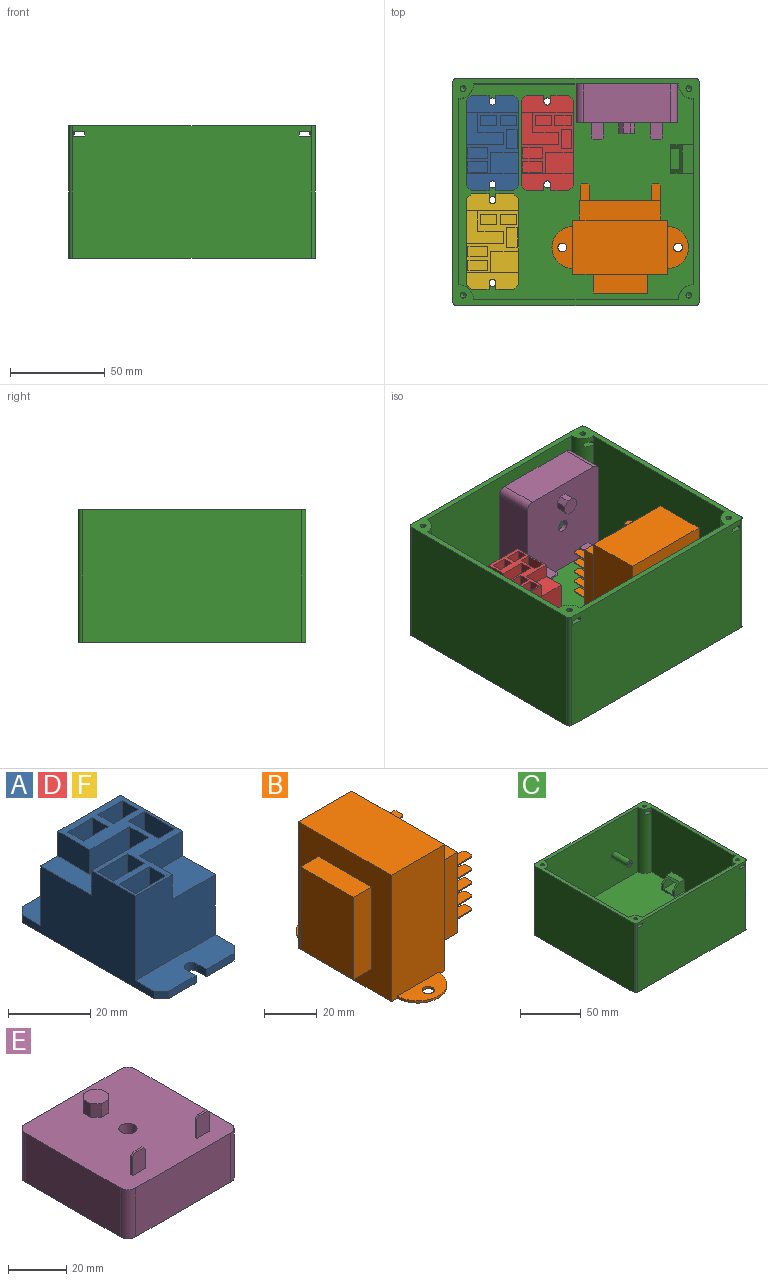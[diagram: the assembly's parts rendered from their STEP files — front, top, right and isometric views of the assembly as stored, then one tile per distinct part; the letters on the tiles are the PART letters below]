
ASSEMBLY  parts=6 mates=8
PART A: 55 faces, bbox 27.4x50.3x27.3 mm
  f0: plane 9.42x2.2mm, normal (0,-1,0), area 20.7mm2, adj f2,f9,f14,f54
  f1: plane 9.42x2.2mm, normal (0,1,0), area 20.7mm2, adj f3,f9,f13,f50
  f2: plane 27.43x8.89mm, normal (0,0,1), area 220.5mm2, adj f0,f5,f6,f7,f10,f14,f15,f52
  f3: plane 27.43x8.89mm, normal (0,0,1), area 220.5mm2, adj f1,f5,f6,f8,f11,f12,f13,f49
  f4: plane 32.51x27.43mm, normal (0,0,1), area 270.6mm2, adj f5,f6,f7,f8,f16,f17,f18,f19
  f5: plane 45.29x27.3mm, normal (1,0,0), area 833.8mm2, adj f2,f3,f4,f7,f8,f9,f13,f14
  f6: plane 45.29x27.3mm, normal (-1,0,0), area 789mm2, adj f2,f3,f4,f7,f8,f9,f12,f15
  f7: plane 27.43x25.1mm, normal (0,-1,0), area 581mm2, adj f2,f4,f5,f6,f21,f23
  f8: plane 27.43x25.1mm, normal (0,1,0), area 645.2mm2, adj f3,f4,f5,f6,f17,f20
  f9: plane 50.29x27.43mm, normal (0,0,-1), area 1332.8mm2, adj f0,f1,f5,f6,f10,f11,f12,f13
  f10: plane 9.42x2.2mm, normal (0,-1,0), area 20.7mm2, adj f2,f9,f15,f53
  f11: plane 9.42x2.2mm, normal (0,1,0), area 20.7mm2, adj f3,f9,f12,f51
  f12: plane 2.5x2.5mm, normal (-0.71,0.71,0), area 7.8mm2, adj f3,f6,f9,f11
  f13: plane 2.5x2.5mm, normal (0.71,0.71,0), area 7.8mm2, adj f1,f3,f5,f9
  f14: plane 2.5x2.5mm, normal (0.71,-0.71,0), area 7.8mm2, adj f0,f2,f5,f9
  f15: plane 2.5x2.5mm, normal (-0.71,-0.71,0), area 7.8mm2, adj f2,f6,f9,f10
  f16: plane 13.7x7.3mm, normal (0,-1,0), area 100mm2, adj f4,f17,f19,f20
  f17: plane 10.96x7.3mm, normal (-1,0,0), area 80mm2, adj f4,f8,f16,f20
  f18: plane 19.63x7.3mm, normal (0,1,0), area 143.3mm2, adj f4,f6,f19,f20
  f19: plane 7.3x6.4mm, normal (-1,0,0), area 46.7mm2, adj f4,f16,f18,f20
  f20: plane 19.63x17.36mm, normal (0,0,1), area 190.7mm2, adj f6,f8,f16,f17,f18,f19
  f21: plane 11.21x7.3mm, normal (1,0,0), area 81.8mm2, adj f4,f7,f22,f23
  f22: plane 14.73x7.3mm, normal (0,-1,0), area 107.5mm2, adj f4,f5,f21,f23
  f23: plane 14.73x11.21mm, normal (0,0,1), area 165.2mm2, adj f5,f7,f21,f22
  f24: plane 7.3x5.3mm, normal (1,0,0), area 38.7mm2, adj f4,f25,f27,f28
  f25: plane 8.5x7.3mm, normal (0,1,0), area 62.1mm2, adj f4,f24,f26,f28
  f26: plane 7.3x5.3mm, normal (-1,0,0), area 38.7mm2, adj f4,f25,f27,f28
  f27: plane 8.5x7.3mm, normal (0,-1,0), area 62.1mm2, adj f4,f24,f26,f28
  f28: plane 8.5x5.3mm, normal (0,0,1), area 45.1mm2, adj f24,f25,f26,f27
  f29: plane 8.5x7.3mm, normal (0,-1,0), area 62.1mm2, adj f4,f30,f32,f33
  f30: plane 7.3x5.3mm, normal (1,0,0), area 38.7mm2, adj f4,f29,f31,f33
  f31: plane 8.5x7.3mm, normal (0,1,0), area 62.1mm2, adj f4,f30,f32,f33
  f32: plane 7.3x5.3mm, normal (-1,0,0), area 38.7mm2, adj f4,f29,f31,f33
  f33: plane 8.5x5.3mm, normal (0,0,1), area 45.1mm2, adj f29,f30,f31,f32
  f34: plane 7.3x5.6mm, normal (0,1,0), area 40.9mm2, adj f4,f35,f37,f38
  f35: plane 10.3x7.3mm, normal (-1,0,0), area 75.2mm2, adj f4,f34,f36,f38
  f36: plane 7.3x5.6mm, normal (0,-1,0), area 40.9mm2, adj f4,f35,f37,f38
  f37: plane 10.3x7.3mm, normal (1,0,0), area 75.2mm2, adj f4,f34,f36,f38
  f38: plane 10.3x5.6mm, normal (0,0,1), area 57.7mm2, adj f34,f35,f36,f37
  f39: plane 10.5x7.3mm, normal (0,-1,0), area 76.7mm2, adj f4,f40,f42,f43
  f40: plane 7.3x5.6mm, normal (1,0,0), area 40.9mm2, adj f4,f39,f41,f43
  f41: plane 10.5x7.3mm, normal (0,1,0), area 76.6mm2, adj f4,f40,f42,f43
  f42: plane 7.3x5.6mm, normal (-1,0,0), area 40.9mm2, adj f4,f39,f41,f43
  f43: plane 10.5x5.6mm, normal (0,0,1), area 58.8mm2, adj f39,f40,f41,f42
  f44: plane 10.5x7.3mm, normal (0,-1,0), area 76.7mm2, adj f4,f45,f47,f48
  f45: plane 7.3x5.6mm, normal (1,0,0), area 40.9mm2, adj f4,f44,f46,f48
  f46: plane 10.5x7.3mm, normal (0,1,0), area 76.7mm2, adj f4,f45,f47,f48
  f47: plane 7.3x5.6mm, normal (-1,0,0), area 40.9mm2, adj f4,f44,f46,f48
  f48: plane 10.5x5.6mm, normal (0,0,1), area 58.8mm2, adj f44,f45,f46,f47
  f49: cylinder r=1.8mm len=3.6mm, axis (0,0,-1), area 12.4mm2, adj f3,f9,f50,f51
  f50: plane 3.35x2.2mm, normal (-1,0,0), area 7.4mm2, adj f1,f3,f9,f49
  f51: plane 3.35x2.2mm, normal (1,0,0), area 7.4mm2, adj f3,f9,f11,f49
  f52: cylinder r=1.8mm len=3.6mm, axis (0,0,-1), area 12.4mm2, adj f2,f9,f53,f54
  f53: plane 3.35x2.2mm, normal (1,0,0), area 7.4mm2, adj f2,f9,f10,f52
  f54: plane 3.35x2.2mm, normal (-1,0,0), area 7.4mm2, adj f0,f2,f9,f52
PART B: 92 faces, bbox 57.7x72x58.8 mm
  f0: plane 58.75x49.85mm, normal (1,0,0), area 1316.2mm2, adj f1,f3,f4,f5,f17,f18,f19,f20
  f1: plane 58.75x28.65mm, normal (0,1,0), area 1661.1mm2, adj f0,f2,f4,f5,f10,f11
  f2: plane 58.75x49.85mm, normal (-1,0,0), area 1838.6mm2, adj f1,f3,f4,f5,f12,f13,f14,f15
  f3: plane 58.75x28.65mm, normal (0,-1,0), area 1661.1mm2, adj f0,f2,f4,f5,f6,f8
  f4: plane 49.85x28.65mm, normal (0,0,1), area 1428.2mm2, adj f0,f1,f2,f3
  f5: plane 71.95x28.65mm, normal (0,0,-1), area 1777.1mm2, adj f0,f1,f2,f3,f6,f7,f9,f10
  f6: cylinder r=11.05mm len=22.1mm, axis (0,0,-1), area 34.7mm2, adj f3,f5,f8
  f7: cylinder r=2.35mm len=4.7mm, axis (0,0,-1), area 14.8mm2, adj f5,f8
  f8: plane 22.1x11.05mm, normal (0,0,1), area 174.4mm2, adj f3,f6,f7
  f9: cylinder r=2.35mm len=4.7mm, axis (0,0,-1), area 14.8mm2, adj f5,f11
  f10: cylinder r=11.05mm len=22.1mm, axis (0,0,-1), area 34.7mm2, adj f1,f5,f11
  f11: plane 22.1x11.05mm, normal (0,0,1), area 174.4mm2, adj f1,f9,f10
  f12: plane 38.25x9.75mm, normal (0,-1,0), area 372.9mm2, adj f2,f13,f15,f16
  f13: plane 28.5x9.75mm, normal (0,0,1), area 277.9mm2, adj f2,f12,f14,f16
  f14: plane 38.25x9.75mm, normal (0,1,0), area 372.9mm2, adj f2,f13,f15,f16
  f15: plane 28.5x9.75mm, normal (0,0,-1), area 277.9mm2, adj f2,f12,f14,f16
  f16: plane 38.25x28.5mm, normal (-1,0,0), area 1090.1mm2, adj f12,f13,f14,f15
  f17: plane 37.5x10.5mm, normal (0,1,0), area 393.8mm2, adj f0,f18,f20,f21
  f18: plane 43x10.5mm, normal (0,0,1), area 451.5mm2, adj f0,f17,f19,f21
  f19: plane 37.5x10.5mm, normal (0,-1,0), area 393.8mm2, adj f0,f18,f20,f21
  f20: plane 43x10.5mm, normal (0,0,-1), area 451.5mm2, adj f0,f17,f19,f21
  f21: plane 43x37.5mm, normal (1,0,0), area 1588.5mm2, adj f17,f18,f19,f20,f22,f23,f24,f25
  f22: plane 8x0.5mm, normal (0,1,0), area 4mm2, adj f21,f23,f25,f86
  f23: plane 8.75x4.8mm, normal (0,0,1), area 41.4mm2, adj f21,f22,f24,f26,f86,f87
  f24: plane 8x0.5mm, normal (0,-1,0), area 4mm2, adj f21,f23,f25,f87
  f25: plane 8.75x4.8mm, normal (0,0,-1), area 41.4mm2, adj f21,f22,f24,f26,f86,f87
  f26: plane 3.3x0.5mm, normal (1,0,0), area 1.6mm2, adj f23,f25,f86,f87
  f27: plane 8.75x4.8mm, normal (0,0,-1), area 41.4mm2, adj f21,f28,f30,f31,f88,f89
  f28: plane 8x0.5mm, normal (0,1,0), area 4mm2, adj f21,f27,f29,f88
  f29: plane 8.75x4.8mm, normal (0,0,1), area 41.4mm2, adj f21,f28,f30,f31,f88,f89
  f30: plane 8x0.5mm, normal (0,-1,0), area 4mm2, adj f21,f27,f29,f89
  f31: plane 3.3x0.5mm, normal (1,0,0), area 1.7mm2, adj f27,f29,f88,f89
  f32: plane 8.75x4.8mm, normal (0,0,-1), area 41.4mm2, adj f21,f33,f35,f36,f90,f91
  f33: plane 8x0.5mm, normal (0,1,0), area 4mm2, adj f21,f32,f34,f90
  f34: plane 8.75x4.8mm, normal (0,0,1), area 41.4mm2, adj f21,f33,f35,f36,f90,f91
  f35: plane 8x0.5mm, normal (0,-1,0), area 4mm2, adj f21,f32,f34,f91
  f36: plane 3.3x0.5mm, normal (1,0,0), area 1.7mm2, adj f32,f34,f90,f91
  f37: plane 8x0.5mm, normal (0,1,0), area 4mm2, adj f21,f38,f40,f84
  f38: plane 8.75x4.8mm, normal (0,0,1), area 41.4mm2, adj f21,f37,f39,f41,f84,f85
  f39: plane 8x0.5mm, normal (0,-1,0), area 4mm2, adj f21,f38,f40,f85
  f40: plane 8.75x4.8mm, normal (0,0,-1), area 41.4mm2, adj f21,f37,f39,f41,f84,f85
  f41: plane 3.3x0.5mm, normal (1,0,0), area 1.7mm2, adj f38,f40,f84,f85
  f42: plane 8x0.5mm, normal (0,1,0), area 4mm2, adj f21,f43,f45,f75
  f43: plane 8.75x4.8mm, normal (0,0,1), area 41.4mm2, adj f21,f42,f44,f46,f74,f75
  f44: plane 8x0.5mm, normal (0,-1,0), area 4mm2, adj f21,f43,f45,f74
  f45: plane 8.75x4.8mm, normal (0,0,-1), area 41.4mm2, adj f21,f42,f44,f46,f74,f75
  f46: plane 3.3x0.5mm, normal (1,0,0), area 1.7mm2, adj f43,f45,f74,f75
  f47: plane 8x0.5mm, normal (0,-1,0), area 4mm2, adj f21,f48,f50,f81
  f48: plane 8.75x4.8mm, normal (0,0,-1), area 41.4mm2, adj f21,f47,f49,f51,f80,f81
  f49: plane 8x0.5mm, normal (0,1,0), area 4mm2, adj f21,f48,f50,f80
  f50: plane 8.75x4.8mm, normal (0,0,1), area 41.4mm2, adj f21,f47,f49,f51,f80,f81
  f51: plane 3.3x0.5mm, normal (1,0,0), area 1.6mm2, adj f48,f50,f80,f81
  f52: plane 8x0.5mm, normal (0,-1,0), area 4mm2, adj f21,f53,f55,f79
  f53: plane 8.75x4.8mm, normal (0,0,-1), area 41.4mm2, adj f21,f52,f54,f56,f78,f79
  f54: plane 8x0.5mm, normal (0,1,0), area 4mm2, adj f21,f53,f55,f78
  f55: plane 8.75x4.8mm, normal (0,0,1), area 41.4mm2, adj f21,f52,f54,f56,f78,f79
  f56: plane 3.3x0.5mm, normal (1,0,0), area 1.7mm2, adj f53,f55,f78,f79
  f57: plane 8.75x4.8mm, normal (0,0,1), area 41.4mm2, adj f21,f58,f60,f61,f82,f83
  f58: plane 8x0.5mm, normal (0,-1,0), area 4mm2, adj f21,f57,f59,f83
  f59: plane 8.75x4.8mm, normal (0,0,-1), area 41.4mm2, adj f21,f58,f60,f61,f82,f83
  f60: plane 8x0.5mm, normal (0,1,0), area 4mm2, adj f21,f57,f59,f82
  f61: plane 3.3x0.5mm, normal (1,0,0), area 1.7mm2, adj f57,f59,f82,f83
  f62: plane 8x0.5mm, normal (0,1,0), area 4mm2, adj f21,f63,f65,f72
  f63: plane 8.75x4.8mm, normal (0,0,1), area 41.4mm2, adj f21,f62,f64,f66,f72,f73
  f64: plane 8x0.5mm, normal (0,-1,0), area 4mm2, adj f21,f63,f65,f73
  f65: plane 8.75x4.8mm, normal (0,0,-1), area 41.4mm2, adj f21,f62,f64,f66,f72,f73
  f66: plane 3.3x0.5mm, normal (1,0,0), area 1.7mm2, adj f63,f65,f72,f73
  f67: plane 8x0.5mm, normal (0,-1,0), area 4mm2, adj f21,f68,f70,f77
  f68: plane 8.75x4.8mm, normal (0,0,-1), area 41.4mm2, adj f21,f67,f69,f71,f76,f77
  f69: plane 8x0.5mm, normal (0,1,0), area 4mm2, adj f21,f68,f70,f76
  f70: plane 8.75x4.8mm, normal (0,0,1), area 41.4mm2, adj f21,f67,f69,f71,f76,f77
  f71: plane 3.3x0.5mm, normal (1,0,0), area 1.7mm2, adj f68,f70,f76,f77
  f72: plane 0.75x0.75mm, normal (0.71,0.71,0), area 0.5mm2, adj f62,f63,f65,f66
  f73: plane 0.75x0.75mm, normal (0.71,-0.71,0), area 0.5mm2, adj f63,f64,f65,f66
  f74: plane 0.75x0.75mm, normal (0.71,-0.71,0), area 0.5mm2, adj f43,f44,f45,f46
  f75: plane 0.75x0.75mm, normal (0.71,0.71,0), area 0.5mm2, adj f42,f43,f45,f46
  f76: plane 0.75x0.75mm, normal (0.71,0.71,0), area 0.5mm2, adj f68,f69,f70,f71
  f77: plane 0.75x0.75mm, normal (0.71,-0.71,0), area 0.5mm2, adj f67,f68,f70,f71
  f78: plane 0.75x0.75mm, normal (0.71,0.71,0), area 0.5mm2, adj f53,f54,f55,f56
  f79: plane 0.75x0.75mm, normal (0.71,-0.71,0), area 0.5mm2, adj f52,f53,f55,f56
  f80: plane 0.75x0.75mm, normal (0.71,0.71,0), area 0.5mm2, adj f48,f49,f50,f51
  f81: plane 0.75x0.75mm, normal (0.71,-0.71,0), area 0.5mm2, adj f47,f48,f50,f51
  f82: plane 0.75x0.75mm, normal (0.71,0.71,0), area 0.5mm2, adj f57,f59,f60,f61
  f83: plane 0.75x0.75mm, normal (0.71,-0.71,0), area 0.5mm2, adj f57,f58,f59,f61
  f84: plane 0.75x0.75mm, normal (0.71,0.71,0), area 0.5mm2, adj f37,f38,f40,f41
  f85: plane 0.75x0.75mm, normal (0.71,-0.71,0), area 0.5mm2, adj f38,f39,f40,f41
  f86: plane 0.75x0.75mm, normal (0.71,0.71,0), area 0.5mm2, adj f22,f23,f25,f26
  f87: plane 0.75x0.75mm, normal (0.71,-0.71,0), area 0.5mm2, adj f23,f24,f25,f26
  f88: plane 0.75x0.75mm, normal (0.71,0.71,0), area 0.5mm2, adj f27,f28,f29,f31
  f89: plane 0.75x0.75mm, normal (0.71,-0.71,0), area 0.5mm2, adj f27,f29,f30,f31
  f90: plane 0.75x0.75mm, normal (0.71,0.71,0), area 0.5mm2, adj f32,f33,f34,f36
  f91: plane 0.75x0.75mm, normal (0.71,-0.71,0), area 0.5mm2, adj f32,f34,f35,f36
PART C: 73 faces, bbox 130x120x70 mm
  f0: plane 126x70mm, normal (0,1,0), area 8790mm2, adj f12,f13,f14,f15,f59,f60,f61,f62
  f1: cylinder r=1.5mm len=3mm, axis (0,0,1), area 28.3mm2, adj f13,f68
  f2: plane 126x70mm, normal (0,-1,0), area 8790mm2, adj f12,f13,f16,f17,f45,f46,f47,f48
  f3: cylinder r=1.5mm len=3mm, axis (0,0,1), area 28.3mm2, adj f13,f54
  f4: plane 116x70mm, normal (1,0,0), area 7999.1mm2, adj f12,f13,f14,f17,f30,f38,f39,f40
  f5: plane 15x6mm, normal (-1,0,0), area 39.4mm2, adj f6,f35,f36,f38,f39,f41,f42
  f6: plane 124x114mm, normal (0,0,1), area 13642.4mm2, adj f5,f7,f8,f9,f10,f18,f19,f20
  f7: plane 108x65mm, normal (0,1,0), area 7020mm2, adj f6,f13,f31,f34
  f8: plane 98x65mm, normal (-1,0,0), area 6190mm2, adj f6,f13,f32,f34,f35,f36,f37,f50
  f9: plane 108x65mm, normal (0,-1,0), area 6991.7mm2, adj f6,f13,f27,f32,f33
  f10: plane 98x65mm, normal (1,0,0), area 6370mm2, adj f6,f13,f31,f33,f49,f64
  f11: plane 116x70mm, normal (-1,0,0), area 8120mm2, adj f12,f13,f15,f16
  f12: plane 130x120mm, normal (0,0,-1), area 15484mm2, adj f0,f2,f4,f11,f14,f15,f16,f17
  f13: plane 130x120mm, normal (0,0,1), area 1633.4mm2, adj f0,f1,f2,f3,f4,f7,f8,f9
  f14: cylinder r=2mm len=70mm, axis (0,0,-1), area 219.9mm2, adj f0,f4,f12,f13
  f15: cylinder r=2mm len=70mm, axis (0,0,1), area 219.9mm2, adj f0,f11,f12,f13
  f16: cylinder r=2mm len=70mm, axis (0,0,-1), area 219.9mm2, adj f2,f11,f12,f13
  f17: cylinder r=2mm len=70mm, axis (0,0,1), area 219.9mm2, adj f2,f4,f12,f13
  f18: cylinder r=2.55mm len=5.1mm, axis (0,0,1), area 80.1mm2, adj f6,f12
  f19: cylinder r=2.55mm len=5.1mm, axis (0,0,1), area 80.1mm2, adj f6,f12
  f20: cylinder r=1.95mm len=5mm, axis (0,0,1), area 61.3mm2, adj f6,f12
  f21: cylinder r=1.95mm len=5mm, axis (0,0,1), area 61.3mm2, adj f6,f12
  f22: cylinder r=1.95mm len=5mm, axis (0,0,1), area 61.3mm2, adj f6,f12
  f23: cylinder r=1.95mm len=5mm, axis (0,0,1), area 61.3mm2, adj f6,f12
  f24: cylinder r=1.95mm len=5mm, axis (0,0,1), area 61.3mm2, adj f6,f12
  f25: cylinder r=1.95mm len=5mm, axis (0,0,1), area 61.3mm2, adj f6,f12
  f26: cylinder r=0.75mm len=18mm, axis (0,1,0), area 84.8mm2, adj f28,f29
  f27: cylinder r=3mm len=18mm, axis (0,1,0), area 339.3mm2, adj f9,f28
  f28: plane 6x6mm, normal (0,-1,0), area 26.5mm2, adj f26,f27
  f29: plane 1.5x1.5mm, normal (0,-1,0), area 1.8mm2, adj f26
  f30: cylinder r=2.5mm len=10.86mm, axis (-1,0,0), area 150.9mm2, adj f4,f34
  f31: cylinder r=8mm len=65mm, axis (0,0,1), area 801.7mm2, adj f6,f7,f10,f13,f45,f46,f48
  f32: cylinder r=8mm len=65mm, axis (0,0,1), area 801.7mm2, adj f6,f8,f9,f13,f59,f60,f62
  f33: cylinder r=8mm len=65mm, axis (0,0,1), area 801.7mm2, adj f6,f9,f10,f13,f65,f66,f68
  f34: cylinder r=8mm len=65mm, axis (0,0,1), area 778.1mm2, adj f6,f7,f8,f13,f30,f51,f52,f54
  f35: plane 12x12mm, normal (0,-1,0), area 126mm2, adj f5,f6,f8,f37,f42
  f36: plane 12x12mm, normal (0,1,0), area 126mm2, adj f5,f6,f8,f37,f42
  f37: plane 15x6mm, normal (0,0,1), area 90mm2, adj f8,f35,f36,f42
  f38: plane 15x11.25mm, normal (0,0,1), area 168.7mm2, adj f4,f5,f39,f41
  f39: plane 15x9mm, normal (0,1,0), area 124.9mm2, adj f4,f5,f38,f40,f42
  f40: plane 11.25x10.5mm, normal (0,0,-1), area 118.1mm2, adj f4,f39,f41,f42
  f41: plane 15x9mm, normal (0,-1,0), area 124.9mm2, adj f4,f5,f38,f40,f42
  f42: plane 15x6mm, normal (-0.71,0,0.71), area 55.7mm2, adj f5,f35,f36,f37,f39,f40,f41
  f43: cylinder r=1.5mm len=3mm, axis (0,0,1), area 28.3mm2, adj f13,f60
  f44: cylinder r=1.5mm len=3mm, axis (0,0,1), area 28.3mm2, adj f13,f46
  f45: plane 8.81x2.5mm, normal (-1,0,0), area 22mm2, adj f2,f31,f46,f48
  f46: plane 11x6mm, normal (0,0,-1), area 55.2mm2, adj f2,f31,f44,f45,f47,f49
  f47: plane 11x2.5mm, normal (1,0,0), area 27.5mm2, adj f2,f46,f48,f49
  f48: plane 11x6mm, normal (0,0,1), area 55.2mm2, adj f2,f31,f45,f47,f49,f58
  f49: plane 2.5x0.5mm, normal (0,-1,0), area 1.2mm2, adj f10,f46,f47,f48
  f50: plane 2.5x0.5mm, normal (0,-1,0), area 1.3mm2, adj f8,f52,f53,f54
  f51: plane 8.81x2.5mm, normal (1,0,0), area 22mm2, adj f2,f34,f52,f54
  f52: plane 11x6mm, normal (0,0,1), area 55.2mm2, adj f2,f34,f50,f51,f53,f56
  f53: plane 11x2.5mm, normal (-1,0,0), area 27.5mm2, adj f2,f50,f52,f54
  f54: plane 11x6mm, normal (0,0,-1), area 55.2mm2, adj f2,f3,f34,f50,f51,f53
  f55: cone r=0mm half-angle=59deg, axis (0,0,1), area 8.2mm2, adj f56
  f56: cylinder r=1.5mm len=4.5mm, axis (0,0,1), area 42.4mm2, adj f52,f55
  f57: cone r=0mm half-angle=59deg, axis (0,0,1), area 8.2mm2, adj f58
  f58: cylinder r=1.5mm len=4.5mm, axis (0,0,1), area 42.4mm2, adj f48,f57
  f59: plane 8.81x2.5mm, normal (1,0,0), area 22mm2, adj f0,f32,f60,f62
  f60: plane 11x6mm, normal (0,0,-1), area 55.2mm2, adj f0,f32,f43,f59,f61,f63
  f61: plane 11x2.5mm, normal (-1,0,0), area 27.5mm2, adj f0,f60,f62,f63
  f62: plane 11x6mm, normal (0,0,1), area 55.2mm2, adj f0,f32,f59,f61,f63,f72
  f63: plane 2.5x0.5mm, normal (0,1,0), area 1.2mm2, adj f8,f60,f61,f62
  f64: plane 2.5x0.5mm, normal (0,1,0), area 1.3mm2, adj f10,f66,f67,f68
  f65: plane 8.81x2.5mm, normal (-1,0,0), area 22mm2, adj f0,f33,f66,f68
  f66: plane 11x6mm, normal (0,0,1), area 55.2mm2, adj f0,f33,f64,f65,f67,f70
  f67: plane 11x2.5mm, normal (1,0,0), area 27.5mm2, adj f0,f64,f66,f68
  f68: plane 11x6mm, normal (0,0,-1), area 55.2mm2, adj f0,f1,f33,f64,f65,f67
  f69: cone r=0mm half-angle=59deg, axis (0,0,1), area 8.2mm2, adj f70
  f70: cylinder r=1.5mm len=4.5mm, axis (0,0,1), area 42.4mm2, adj f66,f69
  f71: cone r=0mm half-angle=59deg, axis (0,0,1), area 8.2mm2, adj f72
  f72: cylinder r=1.5mm len=4.5mm, axis (0,0,1), area 42.4mm2, adj f62,f71
PART D: same geometry as A
PART E: 34 faces, bbox 53.5x53.5x29.5 mm
  f0: plane 53.5x53.5mm, normal (0,0,1), area 2748.3mm2, adj f1,f2,f3,f4,f5,f6,f7,f8
  f1: cylinder r=3.8mm len=20.5mm, axis (0,0,-1), area 122.4mm2, adj f0,f2,f9,f10
  f2: plane 45.9x20.5mm, normal (0,1,0), area 940.9mm2, adj f0,f1,f3,f10
  f3: cylinder r=3.8mm len=20.5mm, axis (0,0,-1), area 122.4mm2, adj f0,f2,f4,f10
  f4: plane 45.9x20.5mm, normal (-1,0,0), area 940.9mm2, adj f0,f3,f5,f10
  f5: cylinder r=3.8mm len=20.5mm, axis (0,0,-1), area 122.4mm2, adj f0,f4,f6,f10
  f6: plane 45.9x20.5mm, normal (0,-1,0), area 940.9mm2, adj f0,f5,f7,f10
  f7: cylinder r=3.8mm len=20.5mm, axis (0,0,-1), area 122.4mm2, adj f0,f6,f9,f10
  f8: cylinder r=3.1mm len=20.5mm, axis (0,0,-1), area 399.3mm2, adj f0,f10
  f9: plane 45.9x20.5mm, normal (1,0,0), area 940.9mm2, adj f0,f1,f7,f10
  f10: plane 53.5x53.5mm, normal (0,0,-1), area 2819.7mm2, adj f1,f2,f3,f4,f5,f6,f7,f8
  f11: plane 5.6x2.52mm, normal (0.71,0.71,0), area 19.9mm2, adj f0,f12,f18,f19
  f12: plane 5.6x3.56mm, normal (0,1,0), area 19.9mm2, adj f0,f11,f13,f19
  f13: plane 5.6x2.52mm, normal (-0.71,0.71,0), area 19.9mm2, adj f0,f12,f14,f19
  f14: plane 5.6x3.56mm, normal (-1,0,0), area 19.9mm2, adj f0,f13,f15,f19
  f15: plane 5.6x2.52mm, normal (-0.71,-0.71,0), area 19.9mm2, adj f0,f14,f16,f19
  f16: plane 5.6x3.56mm, normal (0,-1,0), area 19.9mm2, adj f0,f15,f17,f19
  f17: plane 5.6x2.52mm, normal (0.71,-0.71,0), area 19.9mm2, adj f0,f16,f18,f19
  f18: plane 5.6x3.56mm, normal (1,0,0), area 19.9mm2, adj f0,f11,f17,f19
  f19: plane 8.6x8.6mm, normal (0,0,1), area 61.3mm2, adj f11,f12,f13,f14,f15,f16,f17,f18
  f20: plane 8x0.8mm, normal (1,0,0), area 6.4mm2, adj f0,f21,f23,f32
  f21: plane 9x6.3mm, normal (0,1,0), area 55.7mm2, adj f0,f20,f22,f24,f32,f33
  f22: plane 8x0.8mm, normal (-1,0,0), area 6.4mm2, adj f0,f21,f23,f33
  f23: plane 9x6.3mm, normal (0,-1,0), area 55.7mm2, adj f0,f20,f22,f24,f32,f33
  f24: plane 4.3x0.8mm, normal (0,0,1), area 3.4mm2, adj f21,f23,f32,f33
  f25: plane 8x0.8mm, normal (-1,0,0), area 6.4mm2, adj f0,f26,f28,f31
  f26: plane 9x6.3mm, normal (0,-1,0), area 55.7mm2, adj f0,f25,f27,f29,f30,f31
  f27: plane 8x0.8mm, normal (1,0,0), area 6.4mm2, adj f0,f26,f28,f30
  f28: plane 9x6.3mm, normal (0,1,0), area 55.7mm2, adj f0,f25,f27,f29,f30,f31
  f29: plane 4.3x0.8mm, normal (0,0,1), area 3.4mm2, adj f26,f28,f30,f31
  f30: plane 1x1mm, normal (0.71,0,0.71), area 1.1mm2, adj f26,f27,f28,f29
  f31: plane 1x1mm, normal (-0.71,0,0.71), area 1.1mm2, adj f25,f26,f28,f29
  f32: plane 1x1mm, normal (0.71,0,0.71), area 1.1mm2, adj f20,f21,f23,f24
  f33: plane 1x1mm, normal (-0.71,0,0.71), area 1.1mm2, adj f21,f22,f23,f24
PART F: same geometry as A
PLACE A t=(-44.14,25.87,5)mm
PLACE B rot(axis=(0,0,1),90deg) t=(23.21,-29.27,5)mm
PLACE C t=(-0.1,-0.04,0)mm
PLACE D t=(-15.23,25.87,5)mm
PLACE E rot(axis=(1,0,0),90deg) t=(26.68,56.96,35.73)mm
PLACE F t=(-44.14,-26.13,5)mm
MATE planar A.f9 <-> C.f6  axis (0,0,-1) through (-44.14,25.87,5)mm
MATE planar B.f5 <-> C.f6  axis (0,0,-1) through (23.21,-29.27,5)mm
MATE parallel B.f16 <-> C.f7  axis (0,-1,0) through (23.21,-53.35,33.87)mm
MATE planar E.f8 <-> C.f26  axis (0,1,0) through (26.68,56.96,35.73)mm
MATE planar D.f9 <-> C.f6  axis (0,0,-1) through (-15.23,25.87,5)mm
MATE planar A.f6 <-> F.f6  axis (-1,0,0) through (-57.85,24.66,16.6)mm
MATE planar F.f9 <-> C.f6  axis (0,0,-1) through (-44.14,-26.13,5)mm
MATE planar D.f7 <-> A.f7  axis (0,-1,0) through (-16.4,9.62,18.1)mm
